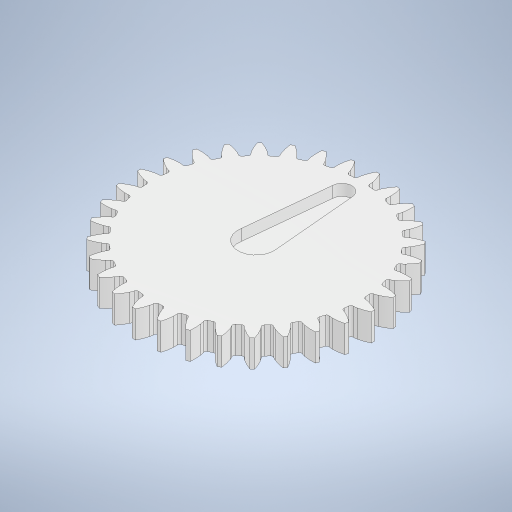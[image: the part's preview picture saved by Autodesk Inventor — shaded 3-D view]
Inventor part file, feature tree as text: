
AUTODESK INVENTOR PART (.ipt)
format: ipt  version: 2023 (Build 270158000, 158)  size: 986,112 bytes
history: mixed  units: in
note: dims shown in document units (in); Inventor stores cm internally (conversion verified against a paired STEP export)
features: extrude x2, move_body x2, delete_face x1, sketch x1, imported_body x1
ambient origin geometry x8: Origin, YZ Plane, XZ Plane, XY Plane, X Axis, Y Axis, Z Axis, Center Point
bodies: Solid1 (imported_parasolid), Body1 (imported_parasolid)
feature tree (7):
  delete_face  "Fläche löschen1"
  sketch  "Skizze1"  dims[d0=0.315in d1=0.0984in d2=0.9921in d3=0.0866in d4=0.0472in d5=0.1102in d6=0.0472in d7=0.1102in d8=0.0472in d9=0.1102in d10=0.0472in d11=0.1102in d12=0.0472in d13=0.1102in d14=0.0472in d15=0.0591in d16=0.2323in d17=0.2008in d18=0.0984in d19=0.0in d20=2.126in d21=0.0394in d22=0.0in d23=0.0687in d24=0.1969in d25=0.0in d26=0.0in]
  extrude  "Extrusion1"  Depth=0.0984in TaperAngle=0.0deg
  extrude  "Extrusion2"  Depth=2.126in
  move_body  "Move Body1"
  move_body  "Move Body2"
  imported_body  NMx_Import_Brep_tag  [imported B-rep: ~4 faces, bbox_mm=None]
